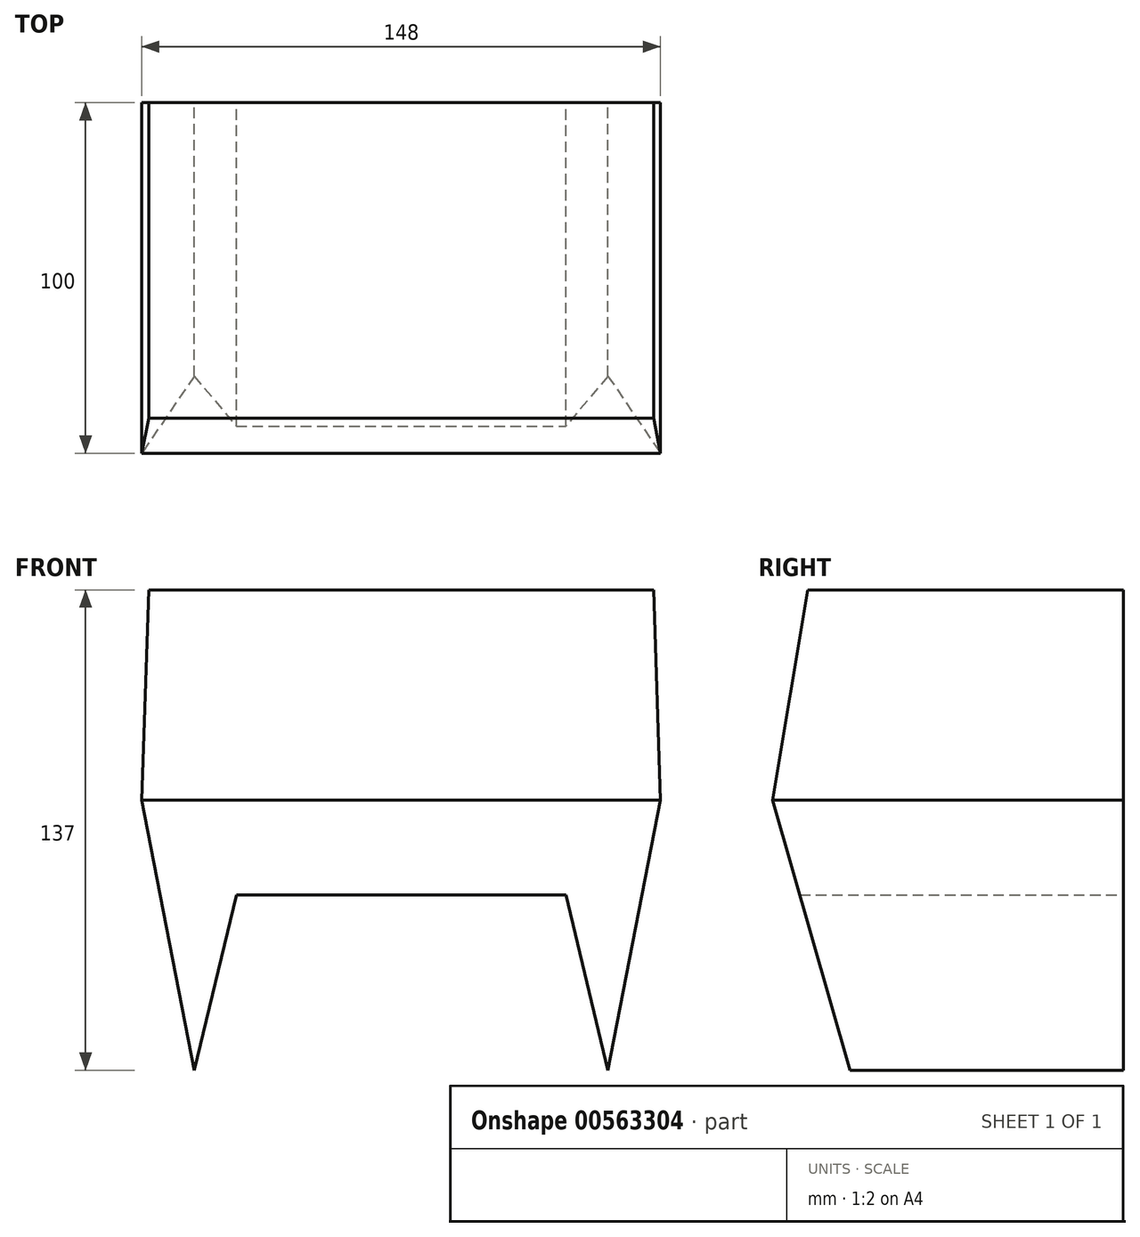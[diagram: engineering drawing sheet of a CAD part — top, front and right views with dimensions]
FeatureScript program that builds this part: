
annotation { "Feature Type Name" : "Feature", "Feature Type Description" : "" }
export const myFeature = defineFeature(function(context is Context, id is Id, definition is map)
    precondition{}
    {
        {
            var Q0;
            Q0=qCreatedBy(makeId("Front.planeOp"),FACE);
            var sketch = newSketch(context, id + "F0", { "sketchPlane" : qUnion([Q0])});
            skLineSegment(sketch, "E0", {"start": v(-62, -12.5) * mm, "end": v(-47, 50) * mm});
            skLineSegment(sketch, "E1", {"start": v(-47, 50) * mm, "end": v(0, 50) * mm});
            skLineSegment(sketch, "E2", {"start": v(-59, 0) * mm, "end": v(-74, 77) * mm});
            skLineSegment(sketch, "E3", {"start": v(-74, 77) * mm, "end": v(-72, 137) * mm});
            skLineSegment(sketch, "E4", {"start": v(-72, 137) * mm, "end": v(0, 137) * mm});
            skLineSegment(sketch, "E5", {"start": v(-74, 77) * mm, "end": v(0, 77) * mm});
            skLineSegment(sketch, "E6.MirrorCS", {"start": v(72, 137) * mm, "end": v(0, 137) * mm});
            skLineSegment(sketch, "E7.MirrorCS", {"start": v(74, 77) * mm, "end": v(72, 137) * mm});
            skLineSegment(sketch, "E8.MirrorCS", {"start": v(74, 77) * mm, "end": v(0, 77) * mm});
            skLineSegment(sketch, "E9.MirrorCS", {"start": v(47, 50) * mm, "end": v(0, 50) * mm});
            skLineSegment(sketch, "E10.MirrorCS", {"start": v(59, 0) * mm, "end": v(74, 77) * mm});
            skLineSegment(sketch, "E11.MirrorCS", {"start": v(62, -12.5) * mm, "end": v(47, 50) * mm});
            skSolve(sketch);
        }
        {
            var Q0;
            Q0=qCreatedBy(makeId("Right.planeOp"),FACE);
            var sketch = newSketch(context, id + "F1", { "sketchPlane" : qUnion([Q0])});
            skLineSegment(sketch, "E12", {"start": v(-45, 137) * mm, "end": v(-55, 77) * mm});
            skLineSegment(sketch, "E13", {"start": v(-55, 77) * mm, "end": v(-33, 0) * mm});
            skLineSegment(sketch, "E14", {"start": v(-45, 137) * mm, "end": v(-80.72, 137) * mm});
            skLineSegment(sketch, "E15", {"start": v(-80.72, 137) * mm, "end": v(-80.72, 0) * mm});
            skLineSegment(sketch, "E16", {"start": v(-80.72, 0) * mm, "end": v(-33, 0) * mm});
            skSolve(sketch);
        }
        {
            var Q0;
            Q0=makeQuery(id+"F0.imprint","IMPRINT",FACE,{"disambiguationData":[TD([[makeQuery(id+"F0.imprint","IMPRINT",EDGE,{"derivedFrom":sQuery(id+"F0.wireOp",EDGE,"E3")}),-1.0]])]});
            var Q1;
            {var subQ1=sQuery(id+"F0.wireOp",EDGE,"E1");Q1=makeQuery(id+"F0.imprint","IMPRINT",FACE,{"disambiguationData":[TD([[makeQuery(id+"F0.imprint","IMPRINT",EDGE,{"derivedFrom":subQ1}),1.0]])]});}
            var Q2;
            Q2=sQuery(id+"F1.wireOp",VERTEX,"E13.start");
            extrude(context, id + "F2", {"entities" : qUnion([Q0, Q1]), "endBound" : BoundingType.UP_TO_VERTEX, "depth" : 25 * mm, "endBoundEntityVertex" : qUnion([Q2]), "offsetDistance" : 25 * mm});
        }
        {
            var Q0;
            Q0 = qSketchRegion(id + "F1", true);
            extrude(context, id + "F3", {"entities" : qUnion([Q0]), "operationType" : NewBodyOperationType.REMOVE, "endBound" : BoundingType.THROUGH_ALL, "oppositeDirection" : true, "depth" : 25 * mm, "offsetDistance" : 25 * mm, "hasSecondDirection" : true, "secondDirectionBound" : SecondDirectionBoundingType.THROUGH_ALL, "secondDirectionOppositeDirection" : false, "secondDirectionDepth" : 25 * mm});
        }
        {
            var Q0;
            Q0=makeQuery(id+"F2.opExtrude","CAP_FACE",FACE,{"disambiguationData":[OSD([sQuery(id+"F0.wireOp",EDGE,"E0"),sQuery(id+"F0.wireOp",EDGE,"E1"),sQuery(id+"F0.wireOp",EDGE,"E2"),sQuery(id+"F0.wireOp",EDGE,"E3"),sQuery(id+"F0.wireOp",EDGE,"E4"),sQuery(id+"F0.wireOp",EDGE,"E6.MirrorCS"),sQuery(id+"F0.wireOp",EDGE,"E7.MirrorCS"),sQuery(id+"F0.wireOp",EDGE,"E9.MirrorCS"),sQuery(id+"F0.wireOp",EDGE,"E10.MirrorCS"),sQuery(id+"F0.wireOp",EDGE,"E11.MirrorCS")])],"isStart":true});
            extrude(context, id + "F4", {"entities" : qUnion([Q0]), "operationType" : NewBodyOperationType.ADD, "depth" : 45 * mm, "offsetDistance" : 25 * mm});
        }
    });
